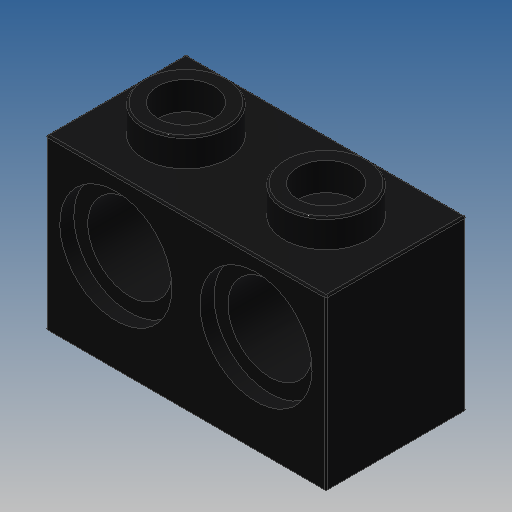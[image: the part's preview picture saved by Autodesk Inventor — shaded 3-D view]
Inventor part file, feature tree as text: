
AUTODESK INVENTOR PART (.ipt)
format: ipt  version: 2022.2 (Build 262287000, 287)  size: 363,520 bytes
history: native  units: in
note: dims shown in document units (in); Inventor stores cm internally (conversion verified against a paired STEP export)
features: sketch x6, extrude x4, fillet x2, pattern_linear x2, other x1, plane x1, revolve x1
ambient origin geometry x8: Origin, YZ Plane, XZ Plane, XY Plane, X Axis, Y Axis, Z Axis, Center Point
bodies: Solid1 (feature_tree)
feature tree (17):
  extrude  "Extrusion1"  Depth=0.378in
  extrude  "Extrusion4"  Depth=0.0039in
  extrude  "Extrusion5"  Depth=0.6299in
  extrude  "Extrusion3"  Depth=0.0591in
  other  "LEGO_SM:1"
  fillet  "Fillet1"  Radius=0.0591in
  pattern_linear  "Rectangular Pattern2"  Count1=2  [1 undecoded]
  fillet  "Fillet2"  Radius=0.315in
  plane  "Work Plane1"
  revolve  "Revolution1"  [1 undecoded]
  pattern_linear  "Rectangular Pattern4"  Spacing1=0.2205in  [1 undecoded]
  sketch  "Sketch2"  dims[d4=0.378in d5=0.0in d13=0.189in]
  sketch  "Sketch4"  dims[d20=0.063in d21=0.0in d23=0.0039in]
  sketch  "Sketch9"  dims[d57=0.126in d58=0.6299in]
  sketch  "Sketch10"  dims[d59=0.315in d61=0.0591in d62=0.0591in]
  sketch  "Sketch11"  dims[d63=0.315in d64=0.0in]
  sketch  "Sketch12"  dims[d69=0.1575in d70=0.7874in d72=0.315in d73=0.0039in d75=0.2205in d76=0.0315in d77=0.189in d78=0.252in d79=90.0deg d83=0.0in d84=0.0in d85=0.0in d86=0.0in d87=0.0in d89=-0.1575in d90=0.7874in d92=0.315in d93=0.063in d94=0.1575in d96=0.2835in d97=0.2205in d98=0.315in d99=0.0in d100=0.0055in d101=0.0513in d102=0.0197in d103=0.0245in d104=0.0055in d105=0.0097in d106=0.0197in d107=0.0245in d108=0.0197in d109=0.0111in d110=0.0124in d111=0.0245in d112=0.5428in]
note: 3 required parameter values undecoded (feature->parameter linkage not recoverable at this tier; creation-order binding heuristic only, values carry confidence <= 0.55)